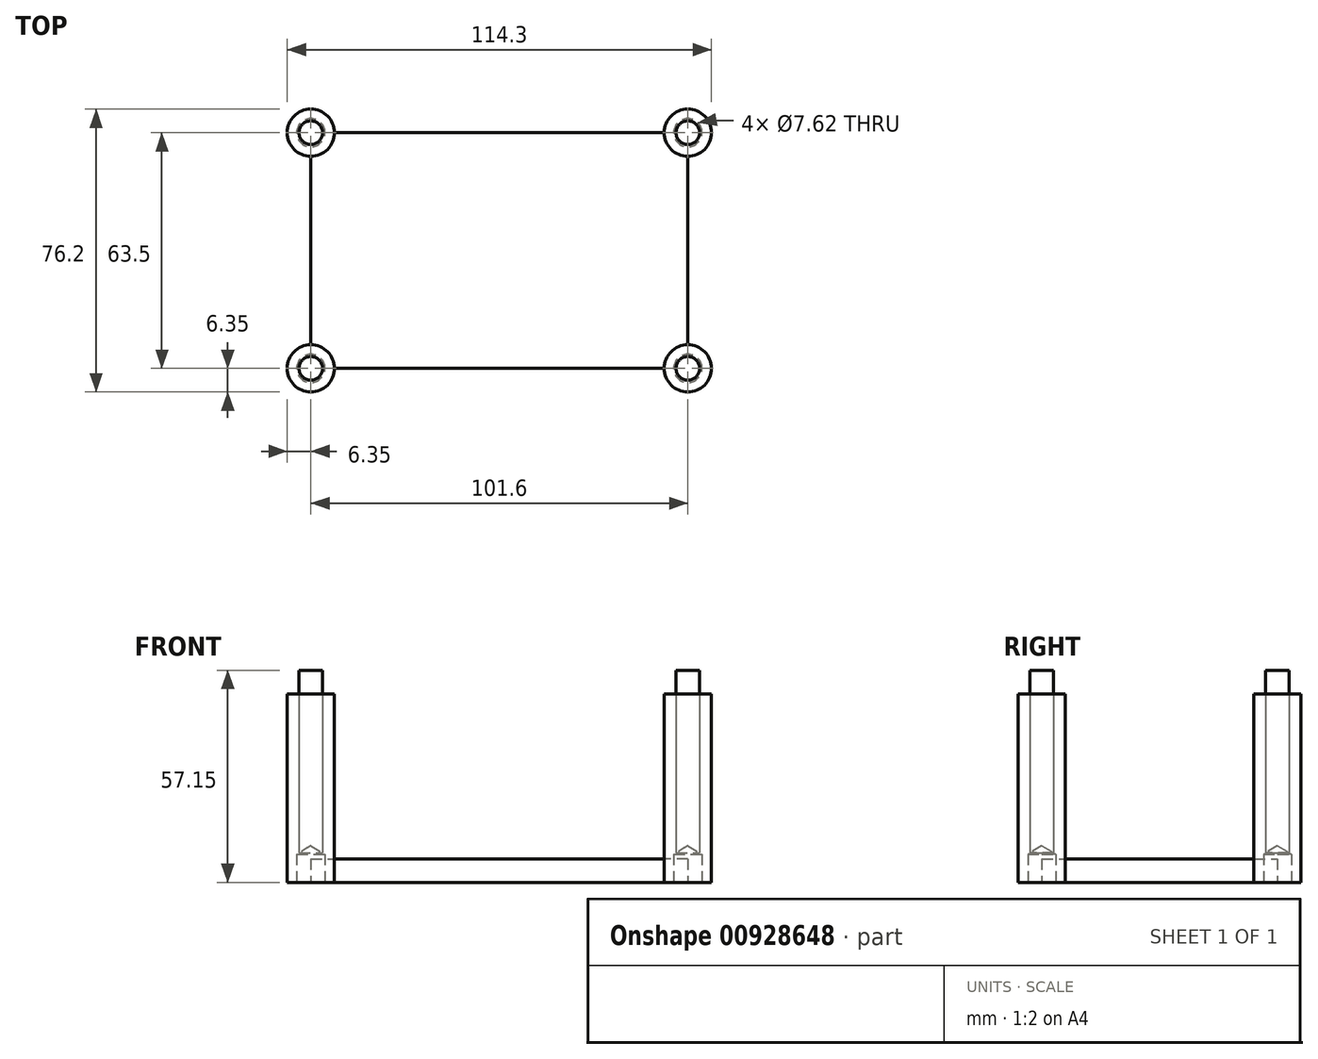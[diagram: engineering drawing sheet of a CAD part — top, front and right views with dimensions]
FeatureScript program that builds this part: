
annotation { "Feature Type Name" : "Feature", "Feature Type Description" : "" }
export const myFeature = defineFeature(function(context is Context, id is Id, definition is map)
    precondition{}
    {
        {
            var Q0;
            Q0=qCreatedBy(makeId("Top.planeOp"),FACE);
            var sketch = newSketch(context, id + "F0", { "sketchPlane" : qUnion([Q0])});
            skLineSegment(sketch, "E0.bottom", {"start": v(50.8, 31.75) * mm, "end": v(-50.8, 31.75) * mm});
            skLineSegment(sketch, "E0.top", {"start": v(50.8, -31.75) * mm, "end": v(-50.8, -31.75) * mm});
            skLineSegment(sketch, "E0.left", {"start": v(50.8, 31.75) * mm, "end": v(50.8, -31.75) * mm});
            skLineSegment(sketch, "E0.right", {"start": v(-50.8, 31.75) * mm, "end": v(-50.8, -31.75) * mm});
            skPoint(sketch, "E0.middle", {"position": v(0, 0) * mm});
            skCircle(sketch, "E1", {"center": v(-50.8, 31.75) * mm, "radius": 6.35 * mm});
            skCircle(sketch, "E2", {"center": v(-50.8, -31.75) * mm, "radius": 6.35 * mm});
            skCircle(sketch, "E3", {"center": v(50.8, -31.75) * mm, "radius": 6.35 * mm});
            skCircle(sketch, "E4", {"center": v(50.8, 31.75) * mm, "radius": 6.35 * mm});
            skCircle(sketch, "E5", {"center": v(-50.8, 31.75) * mm, "radius": 3.18 * mm});
            skCircle(sketch, "E6", {"center": v(-50.8, -31.75) * mm, "radius": 3.18 * mm});
            skCircle(sketch, "E7", {"center": v(50.8, -31.75) * mm, "radius": 3.18 * mm});
            skCircle(sketch, "E8", {"center": v(50.8, 31.75) * mm, "radius": 3.18 * mm});
            skSolve(sketch);
        }
        {
            var Q0;
            {var subQ0=sQuery(id+"F0.wireOp",EDGE,"E1");var subQ1=sQuery(id+"F0.wireOp",EDGE,"E0.bottom");var subQ2=makeQuery(id+"F0.imprint","INTERSECT",VERTEX,{"derivedFrom":[subQ1,subQ0]});Q0=makeQuery(id+"F0.imprint","IMPRINT",FACE,{"disambiguationData":[TD([[makeQuery(id+"F0.imprint","IMPRINT",EDGE,{"disambiguationData":[TD([[subQ2,-1.0]])],"derivedFrom":subQ1}),-1.0]])]});}
            var Q1;
            {var subQ0=sQuery(id+"F0.wireOp",EDGE,"E0.right");var subQ1=sQuery(id+"F0.wireOp",EDGE,"E0.bottom");var subQ2=makeQuery(id+"F0.imprint","INTERSECT",VERTEX,{"derivedFrom":[subQ1,subQ0]});Q1=makeQuery(id+"F0.imprint","IMPRINT",FACE,{"disambiguationData":[TD([[makeQuery(id+"F0.imprint","IMPRINT",EDGE,{"disambiguationData":[TD([[subQ2,1.0]])],"derivedFrom":subQ1}),-1.0]])]});}
            var Q2;
            {var subQ0=sQuery(id+"F0.wireOp",EDGE,"E0.right");var subQ1=sQuery(id+"F0.wireOp",EDGE,"E0.bottom");var subQ2=makeQuery(id+"F0.imprint","INTERSECT",VERTEX,{"derivedFrom":[subQ1,subQ0]});Q2=makeQuery(id+"F0.imprint","IMPRINT",FACE,{"disambiguationData":[TD([[makeQuery(id+"F0.imprint","IMPRINT",EDGE,{"disambiguationData":[TD([[subQ2,1.0]])],"derivedFrom":subQ1}),1.0]])]});}
            var Q3;
            {var subQ0=sQuery(id+"F0.wireOp",EDGE,"E1");var subQ1=sQuery(id+"F0.wireOp",EDGE,"E0.bottom");var subQ2=makeQuery(id+"F0.imprint","INTERSECT",VERTEX,{"derivedFrom":[subQ1,subQ0]});Q3=makeQuery(id+"F0.imprint","IMPRINT",FACE,{"disambiguationData":[TD([[makeQuery(id+"F0.imprint","IMPRINT",EDGE,{"disambiguationData":[TD([[subQ2,-1.0]])],"derivedFrom":subQ1}),1.0]])]});}
            var Q4;
            {var subQ0=sQuery(id+"F0.wireOp",EDGE,"E4");var subQ1=sQuery(id+"F0.wireOp",EDGE,"E0.bottom");var subQ2=makeQuery(id+"F0.imprint","INTERSECT",VERTEX,{"derivedFrom":[subQ1,subQ0]});Q4=makeQuery(id+"F0.imprint","IMPRINT",FACE,{"disambiguationData":[TD([[makeQuery(id+"F0.imprint","IMPRINT",EDGE,{"disambiguationData":[TD([[subQ2,1.0]])],"derivedFrom":subQ1}),1.0]])]});}
            var Q5;
            {var subQ0=sQuery(id+"F0.wireOp",EDGE,"E0.left");var subQ1=sQuery(id+"F0.wireOp",EDGE,"E0.bottom");var subQ2=makeQuery(id+"F0.imprint","INTERSECT",VERTEX,{"derivedFrom":[subQ1,subQ0]});Q5=makeQuery(id+"F0.imprint","IMPRINT",FACE,{"disambiguationData":[TD([[makeQuery(id+"F0.imprint","IMPRINT",EDGE,{"disambiguationData":[TD([[subQ2,-1.0]])],"derivedFrom":subQ1}),1.0]])]});}
            var Q6;
            {var subQ0=sQuery(id+"F0.wireOp",EDGE,"E4");var subQ1=sQuery(id+"F0.wireOp",EDGE,"E0.bottom");var subQ2=makeQuery(id+"F0.imprint","INTERSECT",VERTEX,{"derivedFrom":[subQ1,subQ0]});Q6=makeQuery(id+"F0.imprint","IMPRINT",FACE,{"disambiguationData":[TD([[makeQuery(id+"F0.imprint","IMPRINT",EDGE,{"disambiguationData":[TD([[subQ2,1.0]])],"derivedFrom":subQ1}),-1.0]])]});}
            var Q7;
            {var subQ0=sQuery(id+"F0.wireOp",EDGE,"E0.left");var subQ1=sQuery(id+"F0.wireOp",EDGE,"E0.bottom");var subQ2=makeQuery(id+"F0.imprint","INTERSECT",VERTEX,{"derivedFrom":[subQ1,subQ0]});Q7=makeQuery(id+"F0.imprint","IMPRINT",FACE,{"disambiguationData":[TD([[makeQuery(id+"F0.imprint","IMPRINT",EDGE,{"disambiguationData":[TD([[subQ2,-1.0]])],"derivedFrom":subQ1}),-1.0]])]});}
            var Q8;
            {var subQ0=sQuery(id+"F0.wireOp",EDGE,"E3");var subQ1=sQuery(id+"F0.wireOp",EDGE,"E0.top");var subQ2=makeQuery(id+"F0.imprint","INTERSECT",VERTEX,{"derivedFrom":[subQ1,subQ0]});Q8=makeQuery(id+"F0.imprint","IMPRINT",FACE,{"disambiguationData":[TD([[makeQuery(id+"F0.imprint","IMPRINT",EDGE,{"disambiguationData":[TD([[subQ2,1.0]])],"derivedFrom":subQ1}),-1.0]])]});}
            var Q9;
            {var subQ0=sQuery(id+"F0.wireOp",EDGE,"E3");var subQ1=sQuery(id+"F0.wireOp",EDGE,"E0.top");var subQ2=makeQuery(id+"F0.imprint","INTERSECT",VERTEX,{"derivedFrom":[subQ1,subQ0]});Q9=makeQuery(id+"F0.imprint","IMPRINT",FACE,{"disambiguationData":[TD([[makeQuery(id+"F0.imprint","IMPRINT",EDGE,{"disambiguationData":[TD([[subQ2,1.0]])],"derivedFrom":subQ1}),1.0]])]});}
            var Q10;
            {var subQ0=sQuery(id+"F0.wireOp",EDGE,"E0.left");var subQ1=sQuery(id+"F0.wireOp",EDGE,"E0.top");var subQ2=makeQuery(id+"F0.imprint","INTERSECT",VERTEX,{"derivedFrom":[subQ1,subQ0]});Q10=makeQuery(id+"F0.imprint","IMPRINT",FACE,{"disambiguationData":[TD([[makeQuery(id+"F0.imprint","IMPRINT",EDGE,{"disambiguationData":[TD([[subQ2,-1.0]])],"derivedFrom":subQ1}),1.0]])]});}
            var Q11;
            {var subQ0=sQuery(id+"F0.wireOp",EDGE,"E0.left");var subQ1=sQuery(id+"F0.wireOp",EDGE,"E0.top");var subQ2=makeQuery(id+"F0.imprint","INTERSECT",VERTEX,{"derivedFrom":[subQ1,subQ0]});Q11=makeQuery(id+"F0.imprint","IMPRINT",FACE,{"disambiguationData":[TD([[makeQuery(id+"F0.imprint","IMPRINT",EDGE,{"disambiguationData":[TD([[subQ2,-1.0]])],"derivedFrom":subQ1}),-1.0]])]});}
            var Q12;
            {var subQ0=sQuery(id+"F0.wireOp",EDGE,"E2");var subQ1=sQuery(id+"F0.wireOp",EDGE,"E0.top");var subQ2=makeQuery(id+"F0.imprint","INTERSECT",VERTEX,{"derivedFrom":[subQ1,subQ0]});Q12=makeQuery(id+"F0.imprint","IMPRINT",FACE,{"disambiguationData":[TD([[makeQuery(id+"F0.imprint","IMPRINT",EDGE,{"disambiguationData":[TD([[subQ2,-1.0]])],"derivedFrom":subQ1}),1.0]])]});}
            var Q13;
            {var subQ0=sQuery(id+"F0.wireOp",EDGE,"E0.right");var subQ1=sQuery(id+"F0.wireOp",EDGE,"E0.top");var subQ2=makeQuery(id+"F0.imprint","INTERSECT",VERTEX,{"derivedFrom":[subQ1,subQ0]});Q13=makeQuery(id+"F0.imprint","IMPRINT",FACE,{"disambiguationData":[TD([[makeQuery(id+"F0.imprint","IMPRINT",EDGE,{"disambiguationData":[TD([[subQ2,1.0]])],"derivedFrom":subQ1}),1.0]])]});}
            var Q14;
            {var subQ0=sQuery(id+"F0.wireOp",EDGE,"E0.right");var subQ1=sQuery(id+"F0.wireOp",EDGE,"E0.top");var subQ2=makeQuery(id+"F0.imprint","INTERSECT",VERTEX,{"derivedFrom":[subQ1,subQ0]});Q14=makeQuery(id+"F0.imprint","IMPRINT",FACE,{"disambiguationData":[TD([[makeQuery(id+"F0.imprint","IMPRINT",EDGE,{"disambiguationData":[TD([[subQ2,1.0]])],"derivedFrom":subQ1}),-1.0]])]});}
            var Q15;
            {var subQ0=sQuery(id+"F0.wireOp",EDGE,"E2");var subQ1=sQuery(id+"F0.wireOp",EDGE,"E0.top");var subQ2=makeQuery(id+"F0.imprint","INTERSECT",VERTEX,{"derivedFrom":[subQ1,subQ0]});Q15=makeQuery(id+"F0.imprint","IMPRINT",FACE,{"disambiguationData":[TD([[makeQuery(id+"F0.imprint","IMPRINT",EDGE,{"disambiguationData":[TD([[subQ2,-1.0]])],"derivedFrom":subQ1}),-1.0]])]});}
            extrude(context, id + "F1", {"entities" : qUnion([Q0, Q1, Q2, Q3, Q4, Q5, Q6, Q7, Q8, Q9, Q10, Q11, Q12, Q13, Q14, Q15]), "depth" : 50.8 * mm, "offsetDistance" : 25.4 * mm});
        }
        {
            var Q0;
            {var subQ5=sQuery(id+"F0.wireOp",EDGE,"E4");var subQ13=sQuery(id+"F0.wireOp",EDGE,"E0.bottom");var subQ14=makeQuery(id+"F0.imprint","INTERSECT",VERTEX,{"derivedFrom":[subQ13,subQ5]});Q0=makeQuery(id+"F0.imprint","IMPRINT",FACE,{"disambiguationData":[TD([[makeQuery(id+"F0.imprint","IMPRINT",EDGE,{"disambiguationData":[TD([[subQ14,-1.0]])],"derivedFrom":subQ13}),1.0]])]});}
            extrude(context, id + "F2", {"entities" : qUnion([Q0]), "depth" : 6.35 * mm, "offsetDistance" : 25.4 * mm});
        }
        {
            var Q0;
            {var subQ0=sQuery(id+"F0.wireOp",EDGE,"E0.right");var subQ1=sQuery(id+"F0.wireOp",EDGE,"E0.top");var subQ2=makeQuery(id+"F0.imprint","INTERSECT",VERTEX,{"derivedFrom":[subQ1,subQ0]});Q0=makeQuery(id+"F0.imprint","IMPRINT",FACE,{"disambiguationData":[TD([[makeQuery(id+"F0.imprint","IMPRINT",EDGE,{"disambiguationData":[TD([[subQ2,1.0]])],"derivedFrom":subQ1}),1.0]])]});}
            var Q1;
            {var subQ0=sQuery(id+"F0.wireOp",EDGE,"E0.right");var subQ1=sQuery(id+"F0.wireOp",EDGE,"E0.top");var subQ2=makeQuery(id+"F0.imprint","INTERSECT",VERTEX,{"derivedFrom":[subQ1,subQ0]});Q1=makeQuery(id+"F0.imprint","IMPRINT",FACE,{"disambiguationData":[TD([[makeQuery(id+"F0.imprint","IMPRINT",EDGE,{"disambiguationData":[TD([[subQ2,1.0]])],"derivedFrom":subQ1}),-1.0]])]});}
            var Q2;
            {var subQ0=sQuery(id+"F0.wireOp",EDGE,"E0.right");var subQ1=sQuery(id+"F0.wireOp",EDGE,"E0.bottom");var subQ2=makeQuery(id+"F0.imprint","INTERSECT",VERTEX,{"derivedFrom":[subQ1,subQ0]});Q2=makeQuery(id+"F0.imprint","IMPRINT",FACE,{"disambiguationData":[TD([[makeQuery(id+"F0.imprint","IMPRINT",EDGE,{"disambiguationData":[TD([[subQ2,1.0]])],"derivedFrom":subQ1}),-1.0]])]});}
            var Q3;
            {var subQ0=sQuery(id+"F0.wireOp",EDGE,"E0.right");var subQ1=sQuery(id+"F0.wireOp",EDGE,"E0.bottom");var subQ2=makeQuery(id+"F0.imprint","INTERSECT",VERTEX,{"derivedFrom":[subQ1,subQ0]});Q3=makeQuery(id+"F0.imprint","IMPRINT",FACE,{"disambiguationData":[TD([[makeQuery(id+"F0.imprint","IMPRINT",EDGE,{"disambiguationData":[TD([[subQ2,1.0]])],"derivedFrom":subQ1}),1.0]])]});}
            var Q4;
            {var subQ0=sQuery(id+"F0.wireOp",EDGE,"E0.left");var subQ1=sQuery(id+"F0.wireOp",EDGE,"E0.bottom");var subQ2=makeQuery(id+"F0.imprint","INTERSECT",VERTEX,{"derivedFrom":[subQ1,subQ0]});Q4=makeQuery(id+"F0.imprint","IMPRINT",FACE,{"disambiguationData":[TD([[makeQuery(id+"F0.imprint","IMPRINT",EDGE,{"disambiguationData":[TD([[subQ2,-1.0]])],"derivedFrom":subQ1}),-1.0]])]});}
            var Q5;
            {var subQ0=sQuery(id+"F0.wireOp",EDGE,"E0.left");var subQ1=sQuery(id+"F0.wireOp",EDGE,"E0.bottom");var subQ2=makeQuery(id+"F0.imprint","INTERSECT",VERTEX,{"derivedFrom":[subQ1,subQ0]});Q5=makeQuery(id+"F0.imprint","IMPRINT",FACE,{"disambiguationData":[TD([[makeQuery(id+"F0.imprint","IMPRINT",EDGE,{"disambiguationData":[TD([[subQ2,-1.0]])],"derivedFrom":subQ1}),1.0]])]});}
            var Q6;
            {var subQ0=sQuery(id+"F0.wireOp",EDGE,"E0.left");var subQ1=sQuery(id+"F0.wireOp",EDGE,"E0.top");var subQ2=makeQuery(id+"F0.imprint","INTERSECT",VERTEX,{"derivedFrom":[subQ1,subQ0]});Q6=makeQuery(id+"F0.imprint","IMPRINT",FACE,{"disambiguationData":[TD([[makeQuery(id+"F0.imprint","IMPRINT",EDGE,{"disambiguationData":[TD([[subQ2,-1.0]])],"derivedFrom":subQ1}),1.0]])]});}
            var Q7;
            {var subQ0=sQuery(id+"F0.wireOp",EDGE,"E0.left");var subQ1=sQuery(id+"F0.wireOp",EDGE,"E0.top");var subQ2=makeQuery(id+"F0.imprint","INTERSECT",VERTEX,{"derivedFrom":[subQ1,subQ0]});Q7=makeQuery(id+"F0.imprint","IMPRINT",FACE,{"disambiguationData":[TD([[makeQuery(id+"F0.imprint","IMPRINT",EDGE,{"disambiguationData":[TD([[subQ2,-1.0]])],"derivedFrom":subQ1}),-1.0]])]});}
            extrude(context, id + "F3", {"entities" : qUnion([Q0, Q1, Q2, Q3, Q4, Q5, Q6, Q7]), "depth" : 57.15 * mm, "offsetDistance" : 25.4 * mm});
        }
        {
            var Q0;
            Q0=sQuery(id+"F0.wireOp",VERTEX,"E0.top.end");
            var Q1;
            Q1=sQuery(id+"F0.wireOp",VERTEX,"E0.bottom.end");
            var Q2;
            Q2=sQuery(id+"F0.wireOp",VERTEX,"E0.bottom.start");
            var Q3;
            Q3=sQuery(id+"F0.wireOp",VERTEX,"E0.top.start");
            var Q4;
            Q4=makeQuery(id+"F1.opExtrude","SWEPT_BODY",BODY,{"disambiguationData":[OSD([sQuery(id+"F0.wireOp",EDGE,"E2")])]});
            var Q5;
            Q5=makeQuery(id+"F3.opExtrude","SWEPT_BODY",BODY,{"disambiguationData":[OSD([sQuery(id+"F0.wireOp",EDGE,"E6")])]});
            var Q6;
            Q6=makeQuery(id+"F1.opExtrude","SWEPT_BODY",BODY,{"disambiguationData":[OSD([sQuery(id+"F0.wireOp",EDGE,"E1")])]});
            var Q7;
            Q7=makeQuery(id+"F3.opExtrude","SWEPT_BODY",BODY,{"disambiguationData":[OSD([sQuery(id+"F0.wireOp",EDGE,"E5")])]});
            var Q8;
            Q8=makeQuery(id+"F1.opExtrude","SWEPT_BODY",BODY,{"disambiguationData":[OSD([sQuery(id+"F0.wireOp",EDGE,"E4")])]});
            var Q9;
            Q9=makeQuery(id+"F3.opExtrude","SWEPT_BODY",BODY,{"disambiguationData":[OSD([sQuery(id+"F0.wireOp",EDGE,"E8")])]});
            var Q10;
            Q10=makeQuery(id+"F1.opExtrude","SWEPT_BODY",BODY,{"disambiguationData":[OSD([sQuery(id+"F0.wireOp",EDGE,"E3")])]});
            var Q11;
            Q11=makeQuery(id+"F3.opExtrude","SWEPT_BODY",BODY,{"disambiguationData":[OSD([sQuery(id+"F0.wireOp",EDGE,"E7")])]});
            hole(context, id + "F4", {"style" : HoleStyle.SIMPLE, "endStyle" : HoleEndStyle.BLIND, "oppositeDirection" : true, "holeDiameter" : 7.62 * mm, "majorDiameter" : 6.35 * mm, "holeDepth" : 7.62 * mm, "isTappedThrough" : true, "tappedDepth" : 12.7 * mm, "tapClearance" : 3, "startFromSketch" : true, "locations" : qUnion([Q0, Q1, Q2, Q3]), "scope" : qUnion([Q4, Q5, Q6, Q7, Q8, Q9, Q10, Q11])});
        }
    });
